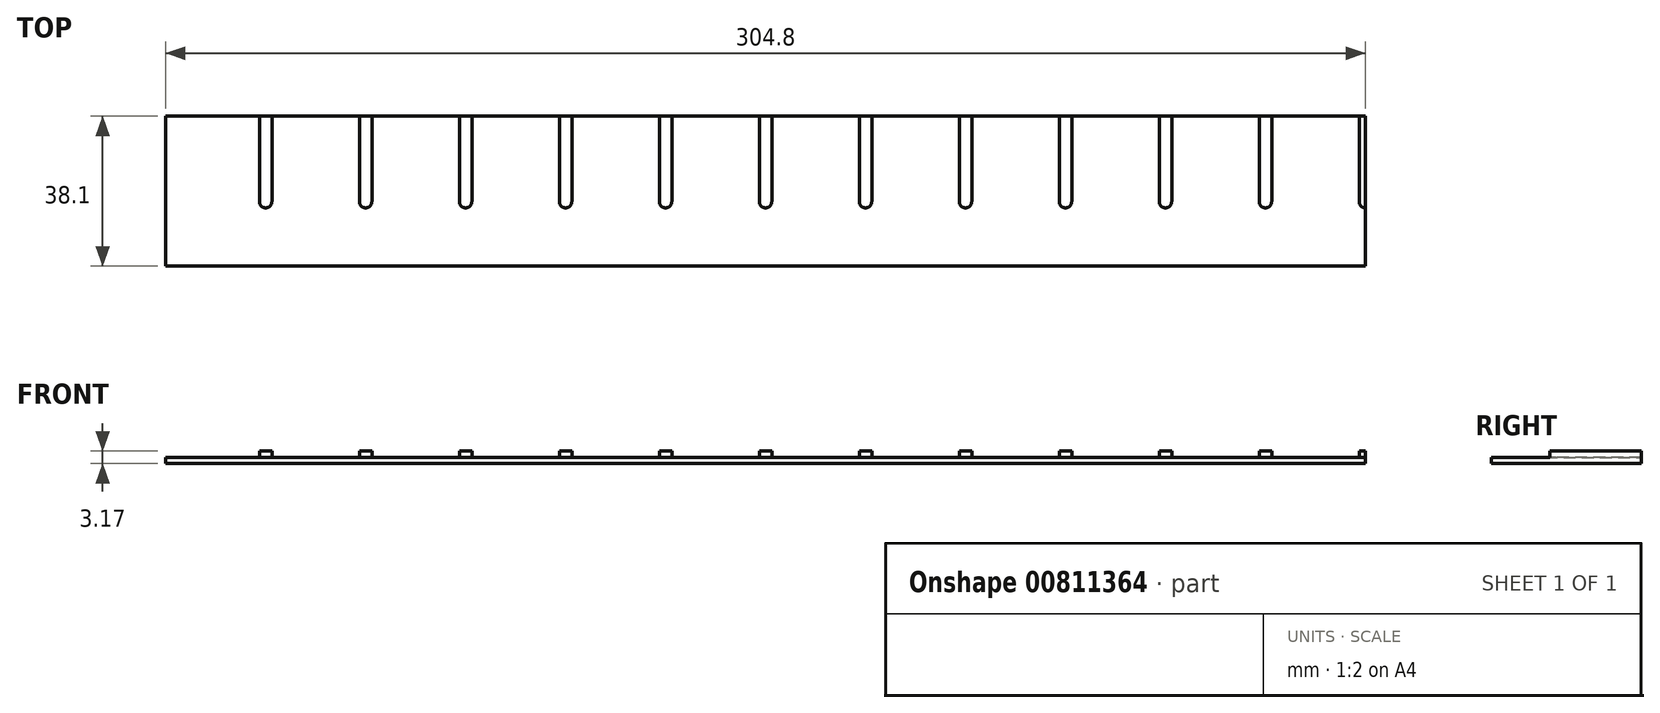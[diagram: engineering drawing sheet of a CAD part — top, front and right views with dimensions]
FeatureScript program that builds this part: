
annotation { "Feature Type Name" : "Feature", "Feature Type Description" : "" }
export const myFeature = defineFeature(function(context is Context, id is Id, definition is map)
    precondition{}
    {
        {
            var Q0;
            Q0=qCreatedBy(makeId("Top.planeOp"),FACE);
            var sketch = newSketch(context, id + "F0", { "sketchPlane" : qUnion([Q0])});
            skLineSegment(sketch, "E0.bottom", {"start": v(-152.12, 0) * mm, "end": v(152.68, 0) * mm});
            skLineSegment(sketch, "E0.top", {"start": v(-152.12, 38.1) * mm, "end": v(152.68, 38.1) * mm});
            skLineSegment(sketch, "E0.left", {"start": v(-152.12, 0) * mm, "end": v(-152.12, 38.1) * mm});
            skLineSegment(sketch, "E0.right", {"start": v(152.68, 0) * mm, "end": v(152.68, 38.1) * mm});
            skSolve(sketch);
        }
        {
            var Q0;
            Q0=makeQuery(id+"F0.imprint","IMPRINT",FACE,{"disambiguationData":[TD([[makeQuery(id+"F0.imprint","IMPRINT",EDGE,{"derivedFrom":sQuery(id+"F0.wireOp",EDGE,"E0.bottom")}),1.0]])]});
            extrude(context, id + "F1", {"entities" : qUnion([Q0]), "depth" : 3.17 * mm, "offsetDistance" : 25.4 * mm});
        }
        {
            var Q0;
            Q0=makeQuery(id+"F1.opExtrude","CAP_FACE",FACE,{"disambiguationData":[OSD([sQuery(id+"F0.wireOp",EDGE,"E0.bottom"),sQuery(id+"F0.wireOp",EDGE,"E0.top"),sQuery(id+"F0.wireOp",EDGE,"E0.left"),sQuery(id+"F0.wireOp",EDGE,"E0.right")])],"isStart":false});
            var sketch = newSketch(context, id + "F2", { "sketchPlane" : qUnion([Q0])});
            skLineSegment(sketch, "E1", {"start": v(-126.72, 38.1) * mm, "end": v(-126.72, 16.4) * mm});
            skLineSegment(sketch, "E2.1.0.0", {"start": v(-101.32, 38.1) * mm, "end": v(-101.32, 16.4) * mm});
            skLineSegment(sketch, "E2.2.0.0", {"start": v(-75.92, 38.1) * mm, "end": v(-75.92, 16.4) * mm});
            skLineSegment(sketch, "E2.3.0.0", {"start": v(-50.52, 38.1) * mm, "end": v(-50.52, 16.4) * mm});
            skLineSegment(sketch, "E2.4.0.0", {"start": v(-25.12, 38.1) * mm, "end": v(-25.12, 16.4) * mm});
            skLineSegment(sketch, "E2.5.0.0", {"start": v(0.28, 38.1) * mm, "end": v(0.28, 16.4) * mm});
            skLineSegment(sketch, "E2.6.0.0", {"start": v(25.68, 38.1) * mm, "end": v(25.68, 16.4) * mm});
            skLineSegment(sketch, "E2.7.0.0", {"start": v(51.08, 38.1) * mm, "end": v(51.08, 16.4) * mm});
            skLineSegment(sketch, "E2.8.0.0", {"start": v(76.48, 38.1) * mm, "end": v(76.48, 16.4) * mm});
            skLineSegment(sketch, "E2.9.0.0", {"start": v(101.88, 38.1) * mm, "end": v(101.88, 16.4) * mm});
            skLineSegment(sketch, "E2.10.0.0", {"start": v(127.28, 38.1) * mm, "end": v(127.28, 16.4) * mm});
            skLineSegment(sketch, "E2.11.0.0", {"start": v(152.68, 38.1) * mm, "end": v(152.68, 16.4) * mm});
            skLineSegment(sketch, "E2.direction1", {"start": v(-126.72, 16.4) * mm, "end": v(-101.32, 16.4) * mm, "construction": true});
            skArc(sketch, "E3.0.startCap", {"start": v(-128.3, 38.1) * mm, "mid": v(-126.72, 39.69) * mm, "end": v(-125.13, 38.1) * mm});
            skArc(sketch, "E3.0.endCap", {"start": v(-125.13, 16.4) * mm, "mid": v(-126.72, 14.81) * mm, "end": v(-128.3, 16.4) * mm});
            skLineSegment(sketch, "E3.0.left", {"start": v(-125.13, 38.1) * mm, "end": v(-125.13, 16.4) * mm});
            skLineSegment(sketch, "E3.0.right", {"start": v(-128.3, 38.1) * mm, "end": v(-128.3, 16.4) * mm});
            skArc(sketch, "E4.0.startCap", {"start": v(-102.9, 38.1) * mm, "mid": v(-101.32, 39.69) * mm, "end": v(-99.73, 38.1) * mm});
            skArc(sketch, "E4.0.endCap", {"start": v(-99.73, 16.4) * mm, "mid": v(-101.32, 14.81) * mm, "end": v(-102.9, 16.4) * mm});
            skLineSegment(sketch, "E4.0.left", {"start": v(-99.73, 38.1) * mm, "end": v(-99.73, 16.4) * mm});
            skLineSegment(sketch, "E4.0.right", {"start": v(-102.9, 38.1) * mm, "end": v(-102.9, 16.4) * mm});
            skArc(sketch, "E4.1.startCap", {"start": v(-77.5, 38.1) * mm, "mid": v(-75.92, 39.69) * mm, "end": v(-74.33, 38.1) * mm});
            skArc(sketch, "E4.1.endCap", {"start": v(-74.33, 16.4) * mm, "mid": v(-75.92, 14.81) * mm, "end": v(-77.5, 16.4) * mm});
            skLineSegment(sketch, "E4.1.left", {"start": v(-74.33, 38.1) * mm, "end": v(-74.33, 16.4) * mm});
            skLineSegment(sketch, "E4.1.right", {"start": v(-77.5, 38.1) * mm, "end": v(-77.5, 16.4) * mm});
            skArc(sketch, "E4.2.startCap", {"start": v(-52.1, 38.1) * mm, "mid": v(-50.52, 39.69) * mm, "end": v(-48.93, 38.1) * mm});
            skArc(sketch, "E4.2.endCap", {"start": v(-48.93, 16.4) * mm, "mid": v(-50.52, 14.81) * mm, "end": v(-52.1, 16.4) * mm});
            skLineSegment(sketch, "E4.2.left", {"start": v(-48.93, 38.1) * mm, "end": v(-48.93, 16.4) * mm});
            skLineSegment(sketch, "E4.2.right", {"start": v(-52.1, 38.1) * mm, "end": v(-52.1, 16.4) * mm});
            skArc(sketch, "E4.3.startCap", {"start": v(-26.7, 38.1) * mm, "mid": v(-25.12, 39.69) * mm, "end": v(-23.53, 38.1) * mm});
            skArc(sketch, "E4.3.endCap", {"start": v(-23.53, 16.4) * mm, "mid": v(-25.12, 14.81) * mm, "end": v(-26.7, 16.4) * mm});
            skLineSegment(sketch, "E4.3.left", {"start": v(-23.53, 38.1) * mm, "end": v(-23.53, 16.4) * mm});
            skLineSegment(sketch, "E4.3.right", {"start": v(-26.7, 38.1) * mm, "end": v(-26.7, 16.4) * mm});
            skArc(sketch, "E4.4.startCap", {"start": v(-1.3, 38.1) * mm, "mid": v(0.28, 39.69) * mm, "end": v(1.87, 38.1) * mm});
            skArc(sketch, "E4.4.endCap", {"start": v(1.87, 16.4) * mm, "mid": v(0.28, 14.81) * mm, "end": v(-1.3, 16.4) * mm});
            skLineSegment(sketch, "E4.4.left", {"start": v(1.87, 38.1) * mm, "end": v(1.87, 16.4) * mm});
            skLineSegment(sketch, "E4.4.right", {"start": v(-1.3, 38.1) * mm, "end": v(-1.3, 16.4) * mm});
            skArc(sketch, "E4.5.startCap", {"start": v(24.1, 38.1) * mm, "mid": v(25.68, 39.69) * mm, "end": v(27.27, 38.1) * mm});
            skArc(sketch, "E4.5.endCap", {"start": v(27.27, 16.4) * mm, "mid": v(25.68, 14.81) * mm, "end": v(24.1, 16.4) * mm});
            skLineSegment(sketch, "E4.5.left", {"start": v(27.27, 38.1) * mm, "end": v(27.27, 16.4) * mm});
            skLineSegment(sketch, "E4.5.right", {"start": v(24.1, 38.1) * mm, "end": v(24.1, 16.4) * mm});
            skArc(sketch, "E4.6.startCap", {"start": v(49.5, 38.1) * mm, "mid": v(51.08, 39.69) * mm, "end": v(52.67, 38.1) * mm});
            skArc(sketch, "E4.6.endCap", {"start": v(52.67, 16.4) * mm, "mid": v(51.08, 14.81) * mm, "end": v(49.5, 16.4) * mm});
            skLineSegment(sketch, "E4.6.left", {"start": v(52.67, 38.1) * mm, "end": v(52.67, 16.4) * mm});
            skLineSegment(sketch, "E4.6.right", {"start": v(49.5, 38.1) * mm, "end": v(49.5, 16.4) * mm});
            skArc(sketch, "E4.7.startCap", {"start": v(74.9, 38.1) * mm, "mid": v(76.48, 39.69) * mm, "end": v(78.07, 38.1) * mm});
            skArc(sketch, "E4.7.endCap", {"start": v(78.07, 16.4) * mm, "mid": v(76.48, 14.81) * mm, "end": v(74.9, 16.4) * mm});
            skLineSegment(sketch, "E4.7.left", {"start": v(78.07, 38.1) * mm, "end": v(78.07, 16.4) * mm});
            skLineSegment(sketch, "E4.7.right", {"start": v(74.9, 38.1) * mm, "end": v(74.9, 16.4) * mm});
            skArc(sketch, "E4.8.startCap", {"start": v(100.3, 38.1) * mm, "mid": v(101.88, 39.69) * mm, "end": v(103.47, 38.1) * mm});
            skArc(sketch, "E4.8.endCap", {"start": v(103.47, 16.4) * mm, "mid": v(101.88, 14.81) * mm, "end": v(100.3, 16.4) * mm});
            skLineSegment(sketch, "E4.8.left", {"start": v(103.47, 38.1) * mm, "end": v(103.47, 16.4) * mm});
            skLineSegment(sketch, "E4.8.right", {"start": v(100.3, 38.1) * mm, "end": v(100.3, 16.4) * mm});
            skArc(sketch, "E4.9.startCap", {"start": v(125.7, 38.1) * mm, "mid": v(127.28, 39.69) * mm, "end": v(128.87, 38.1) * mm});
            skArc(sketch, "E4.9.endCap", {"start": v(128.87, 16.4) * mm, "mid": v(127.28, 14.81) * mm, "end": v(125.7, 16.4) * mm});
            skLineSegment(sketch, "E4.9.left", {"start": v(128.87, 38.1) * mm, "end": v(128.87, 16.4) * mm});
            skLineSegment(sketch, "E4.9.right", {"start": v(125.7, 38.1) * mm, "end": v(125.7, 16.4) * mm});
            skArc(sketch, "E4.10.startCap", {"start": v(151.1, 38.1) * mm, "mid": v(152.68, 39.69) * mm, "end": v(154.27, 38.1) * mm});
            skArc(sketch, "E4.10.endCap", {"start": v(154.27, 16.4) * mm, "mid": v(152.68, 14.81) * mm, "end": v(151.1, 16.4) * mm});
            skLineSegment(sketch, "E4.10.left", {"start": v(154.27, 38.1) * mm, "end": v(154.27, 16.4) * mm});
            skLineSegment(sketch, "E4.10.right", {"start": v(151.1, 38.1) * mm, "end": v(151.1, 16.4) * mm});
            skSolve(sketch);
        }
        {
            var Q0;
            Q0=makeQuery(id+"F2.imprint","IMPRINT",FACE,{"disambiguationData":[TD([[makeQuery(id+"F2.imprint","IMPRINT",EDGE,{"derivedFrom":sQuery(id+"F2.wireOp",EDGE,"E3.0.endCap")}),-1.0]])]});
            var Q1;
            Q1=makeQuery(id+"F2.imprint","IMPRINT",FACE,{"disambiguationData":[TD([[makeQuery(id+"F2.imprint","IMPRINT",EDGE,{"derivedFrom":sQuery(id+"F2.wireOp",EDGE,"E4.0.endCap")}),-1.0]])]});
            var Q2;
            Q2=makeQuery(id+"F2.imprint","IMPRINT",FACE,{"disambiguationData":[TD([[makeQuery(id+"F2.imprint","IMPRINT",EDGE,{"derivedFrom":sQuery(id+"F2.wireOp",EDGE,"E4.1.endCap")}),-1.0]])]});
            var Q3;
            Q3=makeQuery(id+"F2.imprint","IMPRINT",FACE,{"disambiguationData":[TD([[makeQuery(id+"F2.imprint","IMPRINT",EDGE,{"derivedFrom":sQuery(id+"F2.wireOp",EDGE,"E4.2.endCap")}),-1.0]])]});
            var Q4;
            Q4=makeQuery(id+"F2.imprint","IMPRINT",FACE,{"disambiguationData":[TD([[makeQuery(id+"F2.imprint","IMPRINT",EDGE,{"derivedFrom":sQuery(id+"F2.wireOp",EDGE,"E4.3.endCap")}),-1.0]])]});
            var Q5;
            Q5=makeQuery(id+"F2.imprint","IMPRINT",FACE,{"disambiguationData":[TD([[makeQuery(id+"F2.imprint","IMPRINT",EDGE,{"derivedFrom":sQuery(id+"F2.wireOp",EDGE,"E4.4.endCap")}),-1.0]])]});
            var Q6;
            Q6=makeQuery(id+"F2.imprint","IMPRINT",FACE,{"disambiguationData":[TD([[makeQuery(id+"F2.imprint","IMPRINT",EDGE,{"derivedFrom":sQuery(id+"F2.wireOp",EDGE,"E4.5.endCap")}),-1.0]])]});
            var Q7;
            Q7=makeQuery(id+"F2.imprint","IMPRINT",FACE,{"disambiguationData":[TD([[makeQuery(id+"F2.imprint","IMPRINT",EDGE,{"derivedFrom":sQuery(id+"F2.wireOp",EDGE,"E4.6.endCap")}),-1.0]])]});
            var Q8;
            Q8=makeQuery(id+"F2.imprint","IMPRINT",FACE,{"disambiguationData":[TD([[makeQuery(id+"F2.imprint","IMPRINT",EDGE,{"derivedFrom":sQuery(id+"F2.wireOp",EDGE,"E4.7.endCap")}),-1.0]])]});
            var Q9;
            Q9=makeQuery(id+"F2.imprint","IMPRINT",FACE,{"disambiguationData":[TD([[makeQuery(id+"F2.imprint","IMPRINT",EDGE,{"derivedFrom":sQuery(id+"F2.wireOp",EDGE,"E4.8.endCap")}),-1.0]])]});
            var Q10;
            Q10=makeQuery(id+"F2.imprint","IMPRINT",FACE,{"disambiguationData":[TD([[makeQuery(id+"F2.imprint","IMPRINT",EDGE,{"derivedFrom":sQuery(id+"F2.wireOp",EDGE,"E4.9.endCap")}),-1.0]])]});
            extrude(context, id + "F3", {"entities" : qUnion([Q0, Q1, Q2, Q3, Q4, Q5, Q6, Q7, Q8, Q9, Q10]), "operationType" : NewBodyOperationType.REMOVE, "oppositeDirection" : true, "depth" : 1.59 * mm, "offsetDistance" : 25.4 * mm});
        }
        {
            var Q0;
            Q0=makeQuery(id+"F1.opExtrude","CAP_FACE",FACE,{"disambiguationData":[OSD([sQuery(id+"F0.wireOp",EDGE,"E0.bottom"),sQuery(id+"F0.wireOp",EDGE,"E0.top"),sQuery(id+"F0.wireOp",EDGE,"E0.left"),sQuery(id+"F0.wireOp",EDGE,"E0.right")])],"isStart":false});
            var sketch = newSketch(context, id + "F4", { "sketchPlane" : qUnion([Q0])});
            skLineSegment(sketch, "E5", {"start": v(-140.21, 38.1) * mm, "end": v(-140.21, 25.33) * mm});
            skLineSegment(sketch, "E6.1.0.0", {"start": v(-114.81, 38.1) * mm, "end": v(-114.81, 25.33) * mm});
            skLineSegment(sketch, "E6.2.0.0", {"start": v(-89.41, 38.1) * mm, "end": v(-89.41, 25.33) * mm});
            skLineSegment(sketch, "E6.3.0.0", {"start": v(-64.01, 38.1) * mm, "end": v(-64.01, 25.33) * mm});
            skLineSegment(sketch, "E6.4.0.0", {"start": v(-38.61, 38.1) * mm, "end": v(-38.61, 25.33) * mm});
            skLineSegment(sketch, "E6.5.0.0", {"start": v(-13.21, 38.1) * mm, "end": v(-13.21, 25.33) * mm});
            skLineSegment(sketch, "E6.6.0.0", {"start": v(12.19, 38.1) * mm, "end": v(12.19, 25.33) * mm});
            skLineSegment(sketch, "E6.7.0.0", {"start": v(37.59, 38.1) * mm, "end": v(37.59, 25.33) * mm});
            skLineSegment(sketch, "E6.8.0.0", {"start": v(62.99, 38.1) * mm, "end": v(62.99, 25.33) * mm});
            skLineSegment(sketch, "E6.9.0.0", {"start": v(88.39, 38.1) * mm, "end": v(88.39, 25.33) * mm});
            skLineSegment(sketch, "E6.10.0.0", {"start": v(113.79, 38.1) * mm, "end": v(113.79, 25.33) * mm});
            skLineSegment(sketch, "E6.11.0.0", {"start": v(139.19, 38.1) * mm, "end": v(139.19, 25.33) * mm});
            skLineSegment(sketch, "E6.direction1", {"start": v(-140.21, 25.33) * mm, "end": v(-114.81, 25.33) * mm, "construction": true});
            skArc(sketch, "E7.0.startCap", {"start": v(-141, 38.1) * mm, "mid": v(-140.21, 38.9) * mm, "end": v(-139.42, 38.1) * mm});
            skArc(sketch, "E7.0.endCap", {"start": v(-139.42, 25.33) * mm, "mid": v(-140.21, 24.54) * mm, "end": v(-141, 25.33) * mm});
            skLineSegment(sketch, "E7.0.left", {"start": v(-139.42, 38.1) * mm, "end": v(-139.42, 25.33) * mm});
            skLineSegment(sketch, "E7.0.right", {"start": v(-141, 38.1) * mm, "end": v(-141, 25.33) * mm});
            skArc(sketch, "E8.0.startCap", {"start": v(-115.6, 38.1) * mm, "mid": v(-114.81, 38.9) * mm, "end": v(-114.02, 38.1) * mm});
            skArc(sketch, "E8.0.endCap", {"start": v(-114.02, 25.33) * mm, "mid": v(-114.81, 24.54) * mm, "end": v(-115.6, 25.33) * mm});
            skLineSegment(sketch, "E8.0.left", {"start": v(-114.02, 38.1) * mm, "end": v(-114.02, 25.33) * mm});
            skLineSegment(sketch, "E8.0.right", {"start": v(-115.6, 38.1) * mm, "end": v(-115.6, 25.33) * mm});
            skArc(sketch, "E8.1.startCap", {"start": v(-90.2, 38.1) * mm, "mid": v(-89.41, 38.9) * mm, "end": v(-88.62, 38.1) * mm});
            skArc(sketch, "E8.1.endCap", {"start": v(-88.62, 25.33) * mm, "mid": v(-89.41, 24.54) * mm, "end": v(-90.2, 25.33) * mm});
            skLineSegment(sketch, "E8.1.left", {"start": v(-88.62, 38.1) * mm, "end": v(-88.62, 25.33) * mm});
            skLineSegment(sketch, "E8.1.right", {"start": v(-90.2, 38.1) * mm, "end": v(-90.2, 25.33) * mm});
            skArc(sketch, "E8.2.startCap", {"start": v(-64.8, 38.1) * mm, "mid": v(-64.01, 38.9) * mm, "end": v(-63.22, 38.1) * mm});
            skArc(sketch, "E8.2.endCap", {"start": v(-63.22, 25.33) * mm, "mid": v(-64.01, 24.54) * mm, "end": v(-64.8, 25.33) * mm});
            skLineSegment(sketch, "E8.2.left", {"start": v(-63.22, 38.1) * mm, "end": v(-63.22, 25.33) * mm});
            skLineSegment(sketch, "E8.2.right", {"start": v(-64.8, 38.1) * mm, "end": v(-64.8, 25.33) * mm});
            skArc(sketch, "E8.3.startCap", {"start": v(-39.4, 38.1) * mm, "mid": v(-38.61, 38.9) * mm, "end": v(-37.82, 38.1) * mm});
            skArc(sketch, "E8.3.endCap", {"start": v(-37.82, 25.33) * mm, "mid": v(-38.61, 24.54) * mm, "end": v(-39.4, 25.33) * mm});
            skLineSegment(sketch, "E8.3.left", {"start": v(-37.82, 38.1) * mm, "end": v(-37.82, 25.33) * mm});
            skLineSegment(sketch, "E8.3.right", {"start": v(-39.4, 38.1) * mm, "end": v(-39.4, 25.33) * mm});
            skArc(sketch, "E8.4.startCap", {"start": v(-14, 38.1) * mm, "mid": v(-13.21, 38.9) * mm, "end": v(-12.42, 38.1) * mm});
            skArc(sketch, "E8.4.endCap", {"start": v(-12.42, 25.33) * mm, "mid": v(-13.21, 24.54) * mm, "end": v(-14, 25.33) * mm});
            skLineSegment(sketch, "E8.4.left", {"start": v(-12.42, 38.1) * mm, "end": v(-12.42, 25.33) * mm});
            skLineSegment(sketch, "E8.4.right", {"start": v(-14, 38.1) * mm, "end": v(-14, 25.33) * mm});
            skArc(sketch, "E8.5.startCap", {"start": v(11.4, 38.1) * mm, "mid": v(12.19, 38.9) * mm, "end": v(12.98, 38.1) * mm});
            skArc(sketch, "E8.5.endCap", {"start": v(12.98, 25.33) * mm, "mid": v(12.19, 24.54) * mm, "end": v(11.4, 25.33) * mm});
            skLineSegment(sketch, "E8.5.left", {"start": v(12.98, 38.1) * mm, "end": v(12.98, 25.33) * mm});
            skLineSegment(sketch, "E8.5.right", {"start": v(11.4, 38.1) * mm, "end": v(11.4, 25.33) * mm});
            skArc(sketch, "E8.6.startCap", {"start": v(36.8, 38.1) * mm, "mid": v(37.59, 38.9) * mm, "end": v(38.38, 38.1) * mm});
            skArc(sketch, "E8.6.endCap", {"start": v(38.38, 25.33) * mm, "mid": v(37.59, 24.54) * mm, "end": v(36.8, 25.33) * mm});
            skLineSegment(sketch, "E8.6.left", {"start": v(38.38, 38.1) * mm, "end": v(38.38, 25.33) * mm});
            skLineSegment(sketch, "E8.6.right", {"start": v(36.8, 38.1) * mm, "end": v(36.8, 25.33) * mm});
            skArc(sketch, "E8.7.startCap", {"start": v(62.2, 38.1) * mm, "mid": v(62.99, 38.9) * mm, "end": v(63.78, 38.1) * mm});
            skArc(sketch, "E8.7.endCap", {"start": v(63.78, 25.33) * mm, "mid": v(62.99, 24.54) * mm, "end": v(62.2, 25.33) * mm});
            skLineSegment(sketch, "E8.7.left", {"start": v(63.78, 38.1) * mm, "end": v(63.78, 25.33) * mm});
            skLineSegment(sketch, "E8.7.right", {"start": v(62.2, 38.1) * mm, "end": v(62.2, 25.33) * mm});
            skArc(sketch, "E8.8.startCap", {"start": v(87.6, 38.1) * mm, "mid": v(88.39, 38.9) * mm, "end": v(89.18, 38.1) * mm});
            skArc(sketch, "E8.8.endCap", {"start": v(89.18, 25.33) * mm, "mid": v(88.39, 24.54) * mm, "end": v(87.6, 25.33) * mm});
            skLineSegment(sketch, "E8.8.left", {"start": v(89.18, 38.1) * mm, "end": v(89.18, 25.33) * mm});
            skLineSegment(sketch, "E8.8.right", {"start": v(87.6, 38.1) * mm, "end": v(87.6, 25.33) * mm});
            skArc(sketch, "E8.9.startCap", {"start": v(113, 38.1) * mm, "mid": v(113.79, 38.9) * mm, "end": v(114.58, 38.1) * mm});
            skArc(sketch, "E8.9.endCap", {"start": v(114.58, 25.33) * mm, "mid": v(113.79, 24.54) * mm, "end": v(113, 25.33) * mm});
            skLineSegment(sketch, "E8.9.left", {"start": v(114.58, 38.1) * mm, "end": v(114.58, 25.33) * mm});
            skLineSegment(sketch, "E8.9.right", {"start": v(113, 38.1) * mm, "end": v(113, 25.33) * mm});
            skArc(sketch, "E8.10.startCap", {"start": v(138.4, 38.1) * mm, "mid": v(139.19, 38.9) * mm, "end": v(139.98, 38.1) * mm});
            skArc(sketch, "E8.10.endCap", {"start": v(139.98, 25.33) * mm, "mid": v(139.19, 24.54) * mm, "end": v(138.4, 25.33) * mm});
            skLineSegment(sketch, "E8.10.left", {"start": v(139.98, 38.1) * mm, "end": v(139.98, 25.33) * mm});
            skLineSegment(sketch, "E8.10.right", {"start": v(138.4, 38.1) * mm, "end": v(138.4, 25.33) * mm});
            skSolve(sketch);
        }
        {
            var Q0;
            Q0 = qSketchRegion(id + "F4", true);
            extrude(context, id + "F5", {"entities" : qUnion([Q0]), "operationType" : NewBodyOperationType.REMOVE, "oppositeDirection" : true, "depth" : 1.59 * mm, "offsetDistance" : 25.4 * mm});
        }
    });
